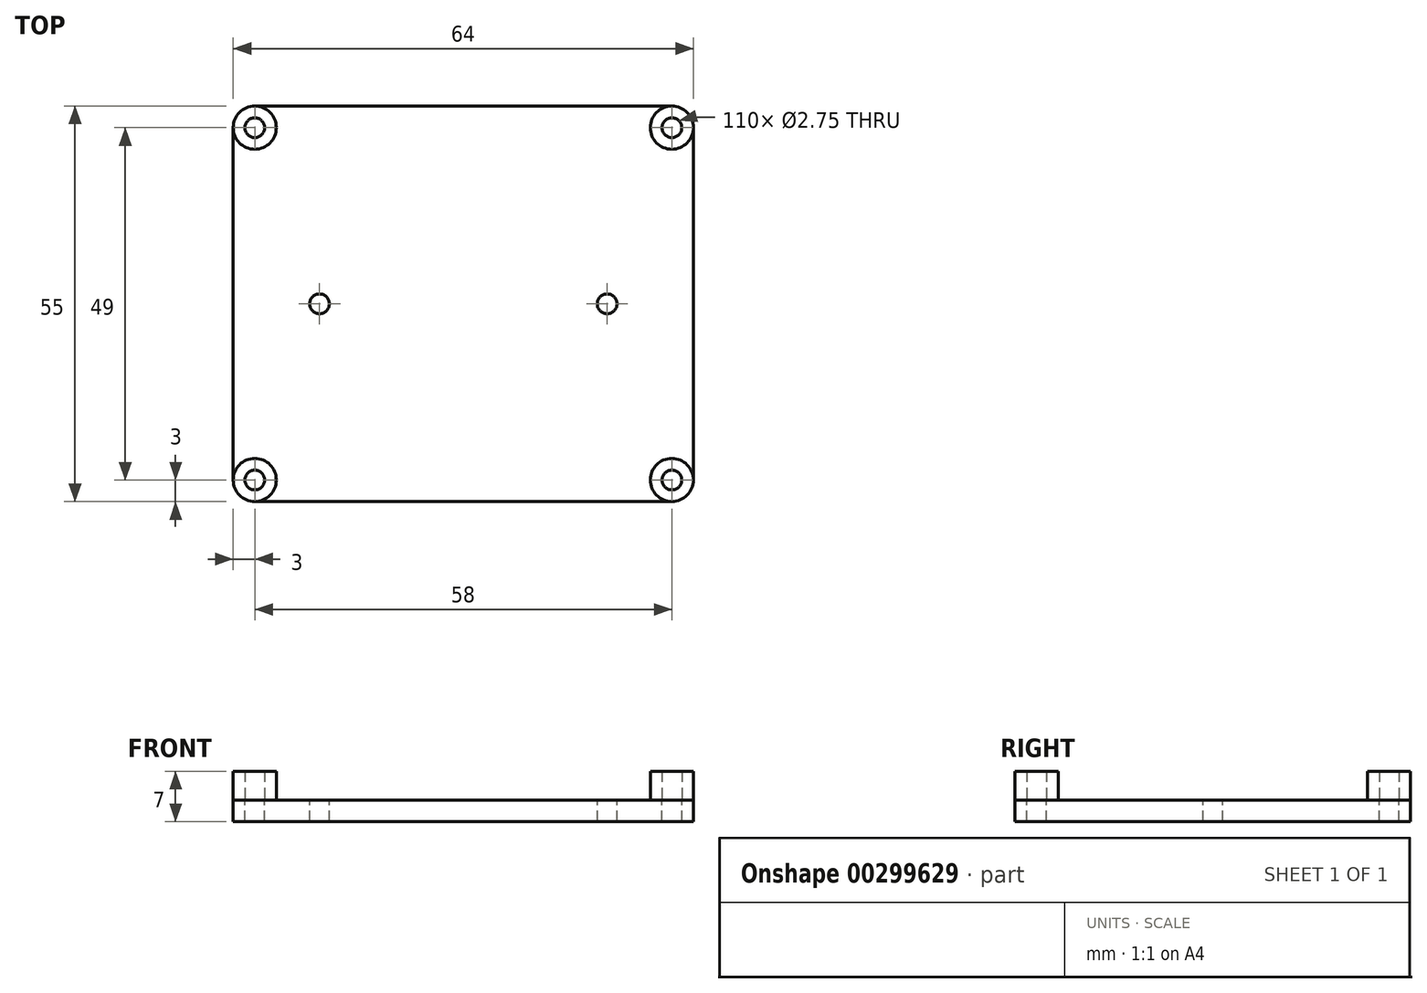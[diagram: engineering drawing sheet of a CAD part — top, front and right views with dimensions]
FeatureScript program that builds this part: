
annotation { "Feature Type Name" : "Feature", "Feature Type Description" : "" }
export const myFeature = defineFeature(function(context is Context, id is Id, definition is map)
    precondition{}
    {
        {
            var Q0;
            Q0=qCreatedBy(makeId("Top.planeOp"),FACE);
            var sketch = newSketch(context, id + "F0", { "sketchPlane" : qUnion([Q0])});
            skLineSegment(sketch, "E0.bottom", {"start": v(-32.8, 27.5) * mm, "end": v(25.2, 27.5) * mm});
            skLineSegment(sketch, "E0.top", {"start": v(-32.8, -27.5) * mm, "end": v(25.2, -27.5) * mm});
            skLineSegment(sketch, "E0.left", {"start": v(-35.8, 24.5) * mm, "end": v(-35.8, -24.5) * mm});
            skLineSegment(sketch, "E0.right", {"start": v(28.2, 24.5) * mm, "end": v(28.2, -24.5) * mm});
            skCircle(sketch, "E1", {"center": v(-32.8, -24.5) * mm, "radius": 3 * mm});
            skCircle(sketch, "E2", {"center": v(-32.8, -24.5) * mm, "radius": 1.38 * mm});
            skCircle(sketch, "E3", {"center": v(25.2, -24.5) * mm, "radius": 3 * mm});
            skCircle(sketch, "E4", {"center": v(25.2, -24.5) * mm, "radius": 1.38 * mm});
            skCircle(sketch, "E5", {"center": v(-32.8, 24.5) * mm, "radius": 3 * mm});
            skCircle(sketch, "E6", {"center": v(-32.8, 24.5) * mm, "radius": 1.38 * mm});
            skCircle(sketch, "E7", {"center": v(25.2, 24.5) * mm, "radius": 3 * mm});
            skCircle(sketch, "E8", {"center": v(25.2, 24.5) * mm, "radius": 1.38 * mm});
            skArc(sketch, "E9.filletArc", {"start": v(28.2, 24.5) * mm, "mid": v(27.32, 26.62) * mm, "end": v(25.2, 27.5) * mm});
            skArc(sketch, "E10.filletArc", {"start": v(-32.8, 27.5) * mm, "mid": v(-34.92, 26.62) * mm, "end": v(-35.8, 24.5) * mm});
            skArc(sketch, "E11.filletArc", {"start": v(-35.8, -24.5) * mm, "mid": v(-34.92, -26.62) * mm, "end": v(-32.8, -27.5) * mm});
            skArc(sketch, "E12.filletArc", {"start": v(25.2, -27.5) * mm, "mid": v(27.32, -26.62) * mm, "end": v(28.2, -24.5) * mm});
            skCircle(sketch, "E13", {"center": v(-23.8, 0) * mm, "radius": 1.38 * mm});
            skCircle(sketch, "E14", {"center": v(16.2, 0) * mm, "radius": 1.38 * mm});
            skSolve(sketch);
        }
        {
            var Q0;
            Q0=makeQuery(id+"F0.imprint","IMPRINT",FACE,{"disambiguationData":[TD([[makeQuery(id+"F0.imprint","IMPRINT",EDGE,{"derivedFrom":sQuery(id+"F0.wireOp",EDGE,"E6")}),-1.0]])]});
            var Q1;
            {var subQ2=sQuery(id+"F0.wireOp",EDGE,"E0.bottom");Q1=makeQuery(id+"F0.imprint","IMPRINT",FACE,{"disambiguationData":[TD([[makeQuery(id+"F0.imprint","IMPRINT",EDGE,{"derivedFrom":subQ2}),-1.0]])]});}
            var Q2;
            Q2=makeQuery(id+"F0.imprint","IMPRINT",FACE,{"disambiguationData":[TD([[makeQuery(id+"F0.imprint","IMPRINT",EDGE,{"derivedFrom":sQuery(id+"F0.wireOp",EDGE,"E2")}),-1.0]])]});
            var Q3;
            Q3=makeQuery(id+"F0.imprint","IMPRINT",FACE,{"disambiguationData":[TD([[makeQuery(id+"F0.imprint","IMPRINT",EDGE,{"derivedFrom":sQuery(id+"F0.wireOp",EDGE,"E4")}),-1.0]])]});
            var Q4;
            Q4=makeQuery(id+"F0.imprint","IMPRINT",FACE,{"disambiguationData":[TD([[makeQuery(id+"F0.imprint","IMPRINT",EDGE,{"derivedFrom":sQuery(id+"F0.wireOp",EDGE,"E8")}),-1.0]])]});
            extrude(context, id + "F1", {"entities" : qUnion([Q0, Q1, Q2, Q3, Q4]), "oppositeDirection" : true, "depth" : 3 * mm});
        }
        {
            var Q0;
            Q0=makeQuery(id+"F0.imprint","IMPRINT",FACE,{"disambiguationData":[TD([[makeQuery(id+"F0.imprint","IMPRINT",EDGE,{"derivedFrom":sQuery(id+"F0.wireOp",EDGE,"E6")}),-1.0]])]});
            var Q1;
            Q1=makeQuery(id+"F0.imprint","IMPRINT",FACE,{"disambiguationData":[TD([[makeQuery(id+"F0.imprint","IMPRINT",EDGE,{"derivedFrom":sQuery(id+"F0.wireOp",EDGE,"E8")}),-1.0]])]});
            var Q2;
            Q2=makeQuery(id+"F0.imprint","IMPRINT",FACE,{"disambiguationData":[TD([[makeQuery(id+"F0.imprint","IMPRINT",EDGE,{"derivedFrom":sQuery(id+"F0.wireOp",EDGE,"E2")}),-1.0]])]});
            var Q3;
            Q3=makeQuery(id+"F0.imprint","IMPRINT",FACE,{"disambiguationData":[TD([[makeQuery(id+"F0.imprint","IMPRINT",EDGE,{"derivedFrom":sQuery(id+"F0.wireOp",EDGE,"E4")}),-1.0]])]});
            extrude(context, id + "F2", {"entities" : qUnion([Q0, Q1, Q2, Q3]), "depth" : 4 * mm});
        }
    });
